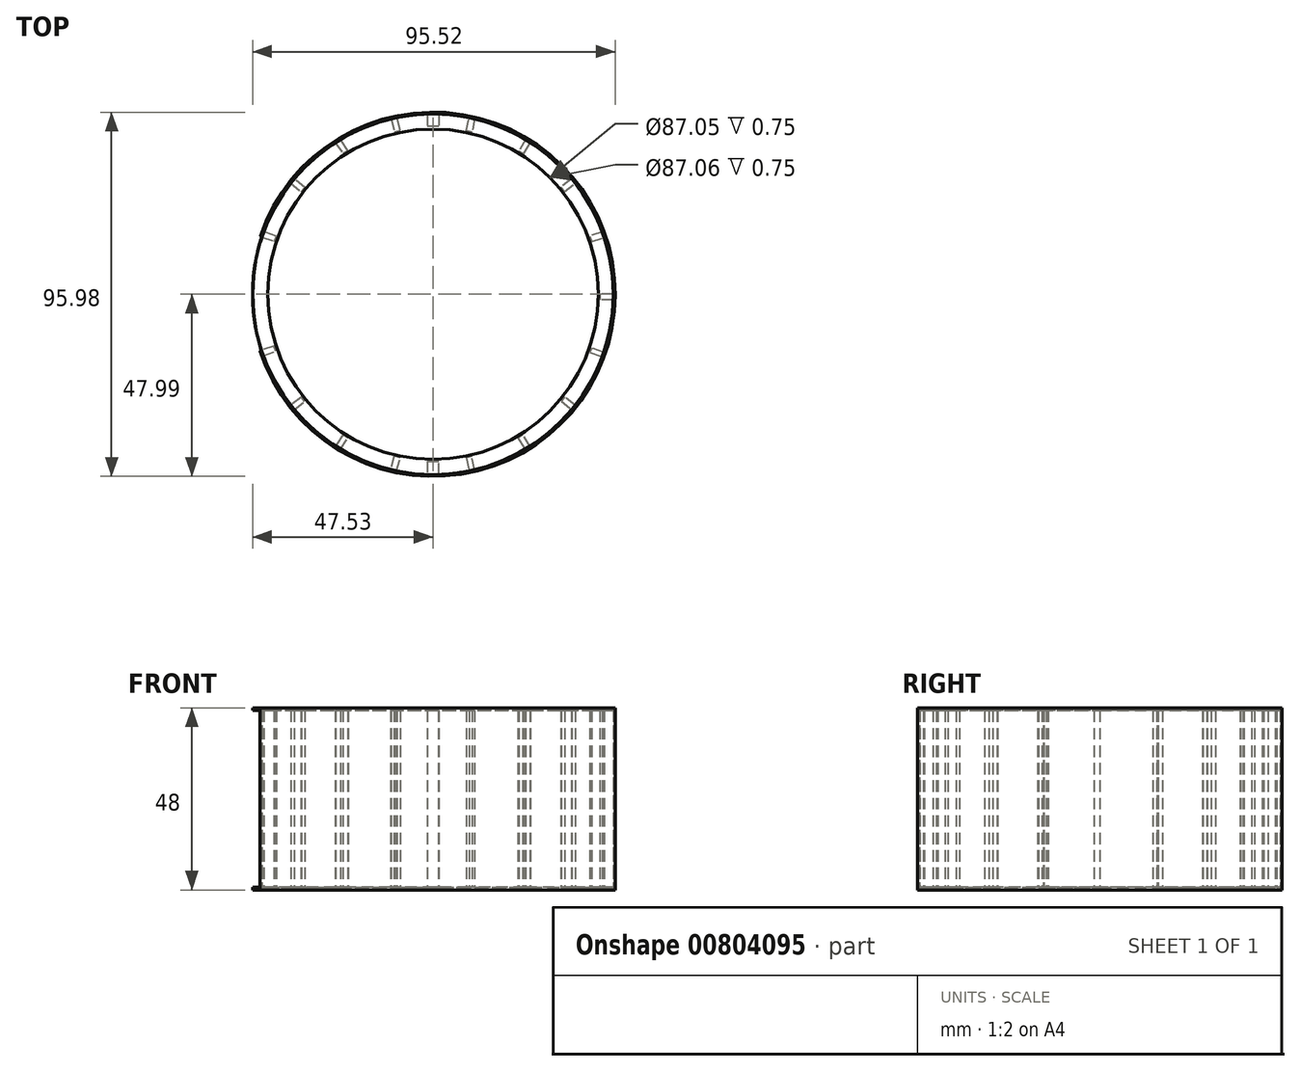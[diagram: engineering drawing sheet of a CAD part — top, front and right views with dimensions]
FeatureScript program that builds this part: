
annotation { "Feature Type Name" : "Feature", "Feature Type Description" : "" }
export const myFeature = defineFeature(function(context is Context, id is Id, definition is map)
    precondition{}
    {
        {
            var Q0;
            Q0=qCreatedBy(makeId("Front.planeOp"),FACE);
            var sketch = newSketch(context, id + "F0", { "sketchPlane" : qUnion([Q0])});
            skLineSegment(sketch, "E0", {"start": v(0, -11.28) * mm, "end": v(0, 12.82) * mm, "construction": true});
            skLineSegment(sketch, "E1", {"start": v(0, 0) * mm, "end": v(47.53, 0) * mm, "construction": true});
            skLineSegment(sketch, "E2.bottom", {"start": v(47.53, 0) * mm, "end": v(43.53, 0) * mm});
            skLineSegment(sketch, "E2.top", {"start": v(47.53, 0.75) * mm, "end": v(43.53, 0.75) * mm});
            skLineSegment(sketch, "E2.left", {"start": v(47.53, 0) * mm, "end": v(47.53, 0.75) * mm});
            skLineSegment(sketch, "E2.right", {"start": v(43.53, 0) * mm, "end": v(43.53, 0.75) * mm});
            skSolve(sketch);
        }
        {
            var Q0;
            Q0 = qSketchRegion(id + "F0", true);
            var Q1;
            Q1=sQuery(id+"F0.wireOp",EDGE,"E0");
            revolve(context, id + "F1", {"surfaceOperationType" : NewSurfaceOperationType.NEW, "entities" : qUnion([Q0]), "axis" : qUnion([Q1]), "revolveType" : RevolveType.FULL});
        }
        {
            var Q0;
            Q0=makeQuery(id+"F1.opRevolve","SWEPT_FACE",FACE,{"disambiguationData":[OSD([sQuery(id+"F0.wireOp",EDGE,"E2.top")])]});
            var sketch = newSketch(context, id + "F2", { "sketchPlane" : qUnion([Q0])});
            skLineSegment(sketch, "E3.bottom", {"start": v(0, 47.5) * mm, "end": v(1.54, 47.5) * mm});
            skLineSegment(sketch, "E3.top", {"start": v(0, 44.24) * mm, "end": v(1.54, 44.24) * mm});
            skLineSegment(sketch, "E3.left", {"start": v(0, 47.5) * mm, "end": v(0, 44.24) * mm});
            skLineSegment(sketch, "E3.right", {"start": v(1.54, 47.5) * mm, "end": v(1.54, 44.24) * mm});
            skLineSegment(sketch, "E4.bottom", {"start": v(0, 47.5) * mm, "end": v(-1.44, 47.5) * mm});
            skLineSegment(sketch, "E4.top", {"start": v(0, 44.24) * mm, "end": v(-1.44, 44.24) * mm});
            skLineSegment(sketch, "E4.right", {"start": v(-1.44, 47.5) * mm, "end": v(-1.44, 44.24) * mm});
            skLineSegment(sketch, "E5.bottom", {"start": v(0, -47.46) * mm, "end": v(1.55, -47.46) * mm});
            skLineSegment(sketch, "E5.top", {"start": v(0, -43.96) * mm, "end": v(1.55, -43.96) * mm});
            skLineSegment(sketch, "E5.left", {"start": v(0, -47.46) * mm, "end": v(0, -43.96) * mm});
            skLineSegment(sketch, "E5.right", {"start": v(1.55, -47.46) * mm, "end": v(1.55, -43.96) * mm});
            skLineSegment(sketch, "E6.bottom", {"start": v(0, -43.96) * mm, "end": v(-1.5, -43.96) * mm});
            skLineSegment(sketch, "E6.top", {"start": v(0, -47.46) * mm, "end": v(-1.5, -47.46) * mm});
            skLineSegment(sketch, "E6.left", {"start": v(0, -43.96) * mm, "end": v(0, -47.46) * mm});
            skLineSegment(sketch, "E6.right", {"start": v(-1.5, -43.96) * mm, "end": v(-1.5, -47.46) * mm});
            skLineSegment(sketch, "E7.bottom", {"start": v(47.53, 0) * mm, "end": v(44.03, 0) * mm});
            skLineSegment(sketch, "E7.top", {"start": v(47.53, -1.5) * mm, "end": v(44.03, -1.5) * mm});
            skLineSegment(sketch, "E7.left", {"start": v(47.53, 0) * mm, "end": v(47.53, -1.5) * mm});
            skLineSegment(sketch, "E7.right", {"start": v(44.03, 0) * mm, "end": v(44.03, -1.5) * mm});
            skLineSegment(sketch, "E8", {"start": v(45.02, -15.26) * mm, "end": v(41.77, -14.12) * mm});
            skLineSegment(sketch, "E9", {"start": v(41.77, -14.12) * mm, "end": v(41.35, -15.32) * mm});
            skLineSegment(sketch, "E10", {"start": v(41.35, -15.32) * mm, "end": v(44.6, -16.45) * mm});
            skLineSegment(sketch, "E11", {"start": v(44.6, -16.45) * mm, "end": v(45.02, -15.26) * mm});
            skLineSegment(sketch, "E12", {"start": v(36.53, -30.4) * mm, "end": v(37.48, -29.23) * mm});
            skLineSegment(sketch, "E13", {"start": v(37.48, -29.23) * mm, "end": v(34.7, -27.03) * mm});
            skLineSegment(sketch, "E14", {"start": v(34.7, -27.03) * mm, "end": v(33.78, -28.2) * mm});
            skLineSegment(sketch, "E15", {"start": v(33.78, -28.2) * mm, "end": v(36.53, -30.4) * mm});
            skLineSegment(sketch, "E16", {"start": v(24.28, -40.86) * mm, "end": v(25.6, -40.05) * mm});
            skLineSegment(sketch, "E17", {"start": v(25.6, -40.05) * mm, "end": v(23.7, -37.06) * mm});
            skLineSegment(sketch, "E18", {"start": v(23.7, -37.06) * mm, "end": v(22.41, -37.87) * mm});
            skLineSegment(sketch, "E19", {"start": v(22.41, -37.87) * mm, "end": v(24.28, -40.86) * mm});
            skLineSegment(sketch, "E20", {"start": v(9.5, -46.57) * mm, "end": v(11, -46.24) * mm});
            skLineSegment(sketch, "E21", {"start": v(11, -46.24) * mm, "end": v(10.25, -42.76) * mm});
            skLineSegment(sketch, "E22", {"start": v(10.25, -42.76) * mm, "end": v(8.77, -43.08) * mm});
            skLineSegment(sketch, "E23", {"start": v(8.77, -43.08) * mm, "end": v(9.5, -46.57) * mm});
            skLineSegment(sketch, "E24", {"start": v(-11.14, -46.2) * mm, "end": v(-9.6, -46.55) * mm});
            skLineSegment(sketch, "E25", {"start": v(-9.6, -46.55) * mm, "end": v(-8.65, -43.13) * mm});
            skLineSegment(sketch, "E26", {"start": v(-8.65, -43.13) * mm, "end": v(-10.27, -42.68) * mm});
            skLineSegment(sketch, "E27", {"start": v(-10.27, -42.68) * mm, "end": v(-11.14, -46.2) * mm});
            skLineSegment(sketch, "E28", {"start": v(-25.65, -40.01) * mm, "end": v(-24.35, -40.82) * mm});
            skLineSegment(sketch, "E29", {"start": v(-24.35, -40.82) * mm, "end": v(-22.39, -37.89) * mm});
            skLineSegment(sketch, "E30", {"start": v(-22.39, -37.89) * mm, "end": v(-23.67, -37.03) * mm});
            skLineSegment(sketch, "E31", {"start": v(-23.67, -37.03) * mm, "end": v(-25.65, -40.01) * mm});
            skLineSegment(sketch, "E32", {"start": v(-37.5, -29.2) * mm, "end": v(-36.51, -30.43) * mm});
            skLineSegment(sketch, "E33", {"start": v(-36.51, -30.43) * mm, "end": v(-33.74, -28.26) * mm});
            skLineSegment(sketch, "E34", {"start": v(-33.74, -28.26) * mm, "end": v(-34.65, -27.08) * mm});
            skLineSegment(sketch, "E35", {"start": v(-34.65, -27.08) * mm, "end": v(-37.5, -29.2) * mm});
            skLineSegment(sketch, "E36", {"start": v(-45.18, -14.77) * mm, "end": v(-44.68, -16.22) * mm});
            skLineSegment(sketch, "E37", {"start": v(-44.68, -16.22) * mm, "end": v(-41.35, -15.08) * mm});
            skLineSegment(sketch, "E38", {"start": v(-41.35, -15.08) * mm, "end": v(-41.84, -13.63) * mm});
            skLineSegment(sketch, "E39", {"start": v(-41.84, -13.63) * mm, "end": v(-45.18, -14.77) * mm});
            skLineSegment(sketch, "E40", {"start": v(-44.58, 16.49) * mm, "end": v(-45.08, 15.07) * mm});
            skLineSegment(sketch, "E41", {"start": v(-45.08, 15.07) * mm, "end": v(-41.75, 13.94) * mm});
            skLineSegment(sketch, "E42", {"start": v(-41.75, 13.94) * mm, "end": v(-41.27, 15.34) * mm});
            skLineSegment(sketch, "E43", {"start": v(-41.27, 15.34) * mm, "end": v(-44.58, 16.49) * mm});
            skLineSegment(sketch, "E44", {"start": v(-36.52, 30.42) * mm, "end": v(-37.46, 29.25) * mm});
            skLineSegment(sketch, "E45", {"start": v(-37.46, 29.25) * mm, "end": v(-34.74, 27) * mm});
            skLineSegment(sketch, "E46", {"start": v(-34.74, 27) * mm, "end": v(-33.78, 28.14) * mm});
            skLineSegment(sketch, "E47", {"start": v(-33.78, 28.14) * mm, "end": v(-36.52, 30.42) * mm});
            skLineSegment(sketch, "E48", {"start": v(-24.42, 40.78) * mm, "end": v(-25.7, 39.98) * mm});
            skLineSegment(sketch, "E49", {"start": v(-25.7, 39.98) * mm, "end": v(-23.7, 37.07) * mm});
            skLineSegment(sketch, "E50", {"start": v(-23.7, 37.07) * mm, "end": v(-22.45, 37.93) * mm});
            skLineSegment(sketch, "E51", {"start": v(-22.45, 37.93) * mm, "end": v(-24.42, 40.78) * mm});
            skLineSegment(sketch, "E52", {"start": v(-9.5, 46.57) * mm, "end": v(-11, 46.24) * mm});
            skLineSegment(sketch, "E53", {"start": v(-11, 46.24) * mm, "end": v(-10.12, 42.8) * mm});
            skLineSegment(sketch, "E54", {"start": v(-10.12, 42.8) * mm, "end": v(-8.66, 43.18) * mm});
            skLineSegment(sketch, "E55", {"start": v(-8.66, 43.18) * mm, "end": v(-9.5, 46.57) * mm});
            skLineSegment(sketch, "E56", {"start": v(9.5, 46.57) * mm, "end": v(10.94, 46.25) * mm});
            skLineSegment(sketch, "E57", {"start": v(10.94, 46.25) * mm, "end": v(10.27, 42.78) * mm});
            skLineSegment(sketch, "E58", {"start": v(10.27, 42.78) * mm, "end": v(8.8, 43.06) * mm});
            skLineSegment(sketch, "E59", {"start": v(8.8, 43.06) * mm, "end": v(9.5, 46.57) * mm});
            skLineSegment(sketch, "E60", {"start": v(25.7, 39.99) * mm, "end": v(24.44, 40.77) * mm});
            skLineSegment(sketch, "E61", {"start": v(24.44, 40.77) * mm, "end": v(22.63, 37.73) * mm});
            skLineSegment(sketch, "E62", {"start": v(22.63, 37.73) * mm, "end": v(23.93, 36.95) * mm});
            skLineSegment(sketch, "E63", {"start": v(23.93, 36.95) * mm, "end": v(25.7, 39.99) * mm});
            skLineSegment(sketch, "E64", {"start": v(37.45, 29.26) * mm, "end": v(36.5, 30.43) * mm});
            skLineSegment(sketch, "E65", {"start": v(36.5, 30.43) * mm, "end": v(33.72, 28.29) * mm});
            skLineSegment(sketch, "E66", {"start": v(33.72, 28.29) * mm, "end": v(34.64, 27.09) * mm});
            skLineSegment(sketch, "E67", {"start": v(34.64, 27.09) * mm, "end": v(37.45, 29.26) * mm});
            skLineSegment(sketch, "E68", {"start": v(45.11, 14.97) * mm, "end": v(44.6, 16.45) * mm});
            skLineSegment(sketch, "E69", {"start": v(44.6, 16.45) * mm, "end": v(41.26, 15.32) * mm});
            skLineSegment(sketch, "E70", {"start": v(41.26, 15.32) * mm, "end": v(41.74, 13.9) * mm});
            skLineSegment(sketch, "E71", {"start": v(41.74, 13.9) * mm, "end": v(45.11, 14.97) * mm});
            skLineSegment(sketch, "E72.bottom", {"start": v(44.03, 0) * mm, "end": v(47.5, 0) * mm});
            skLineSegment(sketch, "E72.top", {"start": v(44.03, 1.5) * mm, "end": v(47.5, 1.5) * mm});
            skLineSegment(sketch, "E72.left", {"start": v(44.03, 0) * mm, "end": v(44.03, 1.5) * mm});
            skLineSegment(sketch, "E72.right", {"start": v(47.5, 0) * mm, "end": v(47.5, 1.5) * mm});
            skSolve(sketch);
        }
        {
            var Q0;
            Q0=makeQuery(id+"F2.imprint","IMPRINT",FACE,{"disambiguationData":[TD([[makeQuery(id+"F2.imprint","IMPRINT",EDGE,{"derivedFrom":sQuery(id+"F2.wireOp",EDGE,"E40")}),1.0]])]});
            var Q1;
            Q1=makeQuery(id+"F2.imprint","IMPRINT",FACE,{"disambiguationData":[TD([[makeQuery(id+"F2.imprint","IMPRINT",EDGE,{"derivedFrom":sQuery(id+"F2.wireOp",EDGE,"E44")}),1.0]])]});
            var Q2;
            Q2=makeQuery(id+"F2.imprint","IMPRINT",FACE,{"disambiguationData":[TD([[makeQuery(id+"F2.imprint","IMPRINT",EDGE,{"derivedFrom":sQuery(id+"F2.wireOp",EDGE,"E48")}),1.0]])]});
            var Q3;
            Q3=makeQuery(id+"F2.imprint","IMPRINT",FACE,{"disambiguationData":[TD([[makeQuery(id+"F2.imprint","IMPRINT",EDGE,{"derivedFrom":sQuery(id+"F2.wireOp",EDGE,"E52")}),1.0]])]});
            var Q4;
            Q4=makeQuery(id+"F2.imprint","IMPRINT",FACE,{"disambiguationData":[TD([[makeQuery(id+"F2.imprint","IMPRINT",EDGE,{"derivedFrom":sQuery(id+"F2.wireOp",EDGE,"E4.bottom")}),1.0]])]});
            var Q5;
            {var subQ1=sQuery(id+"F2.wireOp",EDGE,"E3.top");Q5=makeQuery(id+"F2.imprint","IMPRINT",FACE,{"disambiguationData":[TD([[makeQuery(id+"F2.imprint","IMPRINT",EDGE,{"derivedFrom":subQ1}),1.0]])]});}
            var Q6;
            Q6=makeQuery(id+"F2.imprint","IMPRINT",FACE,{"disambiguationData":[TD([[makeQuery(id+"F2.imprint","IMPRINT",EDGE,{"derivedFrom":sQuery(id+"F2.wireOp",EDGE,"E56")}),-1.0]])]});
            var Q7;
            Q7=makeQuery(id+"F2.imprint","IMPRINT",FACE,{"disambiguationData":[TD([[makeQuery(id+"F2.imprint","IMPRINT",EDGE,{"derivedFrom":sQuery(id+"F2.wireOp",EDGE,"E60")}),1.0]])]});
            var Q8;
            Q8=makeQuery(id+"F2.imprint","IMPRINT",FACE,{"disambiguationData":[TD([[makeQuery(id+"F2.imprint","IMPRINT",EDGE,{"derivedFrom":sQuery(id+"F2.wireOp",EDGE,"E64")}),1.0]])]});
            var Q9;
            Q9=makeQuery(id+"F2.imprint","IMPRINT",FACE,{"disambiguationData":[TD([[makeQuery(id+"F2.imprint","IMPRINT",EDGE,{"derivedFrom":sQuery(id+"F2.wireOp",EDGE,"E68")}),1.0]])]});
            var Q10;
            Q10=makeQuery(id+"F2.imprint","IMPRINT",FACE,{"disambiguationData":[TD([[makeQuery(id+"F2.imprint","IMPRINT",EDGE,{"derivedFrom":sQuery(id+"F2.wireOp",EDGE,"E72.bottom")}),1.0]])]});
            var Q11;
            {var subQ4=sQuery(id+"F2.wireOp",EDGE,"E7.bottom");Q11=makeQuery(id+"F2.imprint","IMPRINT",FACE,{"disambiguationData":[TD([[makeQuery(id+"F2.imprint","IMPRINT",EDGE,{"derivedFrom":subQ4}),1.0]])]});}
            var Q12;
            Q12=makeQuery(id+"F2.imprint","IMPRINT",FACE,{"disambiguationData":[TD([[makeQuery(id+"F2.imprint","IMPRINT",EDGE,{"derivedFrom":sQuery(id+"F2.wireOp",EDGE,"E8")}),1.0]])]});
            var Q13;
            Q13=makeQuery(id+"F2.imprint","IMPRINT",FACE,{"disambiguationData":[TD([[makeQuery(id+"F2.imprint","IMPRINT",EDGE,{"derivedFrom":sQuery(id+"F2.wireOp",EDGE,"E12")}),1.0]])]});
            var Q14;
            Q14=makeQuery(id+"F2.imprint","IMPRINT",FACE,{"disambiguationData":[TD([[makeQuery(id+"F2.imprint","IMPRINT",EDGE,{"derivedFrom":sQuery(id+"F2.wireOp",EDGE,"E16")}),1.0]])]});
            var Q15;
            Q15=makeQuery(id+"F2.imprint","IMPRINT",FACE,{"disambiguationData":[TD([[makeQuery(id+"F2.imprint","IMPRINT",EDGE,{"derivedFrom":sQuery(id+"F2.wireOp",EDGE,"E20")}),1.0]])]});
            var Q16;
            Q16=makeQuery(id+"F2.imprint","IMPRINT",FACE,{"disambiguationData":[TD([[makeQuery(id+"F2.imprint","IMPRINT",EDGE,{"derivedFrom":sQuery(id+"F2.wireOp",EDGE,"E5.bottom")}),1.0]])]});
            var Q17;
            Q17=makeQuery(id+"F2.imprint","IMPRINT",FACE,{"disambiguationData":[TD([[makeQuery(id+"F2.imprint","IMPRINT",EDGE,{"derivedFrom":sQuery(id+"F2.wireOp",EDGE,"E6.bottom")}),1.0]])]});
            var Q18;
            Q18=makeQuery(id+"F2.imprint","IMPRINT",FACE,{"disambiguationData":[TD([[makeQuery(id+"F2.imprint","IMPRINT",EDGE,{"derivedFrom":sQuery(id+"F2.wireOp",EDGE,"E24")}),1.0]])]});
            var Q19;
            Q19=makeQuery(id+"F2.imprint","IMPRINT",FACE,{"disambiguationData":[TD([[makeQuery(id+"F2.imprint","IMPRINT",EDGE,{"derivedFrom":sQuery(id+"F2.wireOp",EDGE,"E28")}),1.0]])]});
            var Q20;
            Q20=makeQuery(id+"F2.imprint","IMPRINT",FACE,{"disambiguationData":[TD([[makeQuery(id+"F2.imprint","IMPRINT",EDGE,{"derivedFrom":sQuery(id+"F2.wireOp",EDGE,"E32")}),1.0]])]});
            var Q21;
            Q21=makeQuery(id+"F2.imprint","IMPRINT",FACE,{"disambiguationData":[TD([[makeQuery(id+"F2.imprint","IMPRINT",EDGE,{"derivedFrom":sQuery(id+"F2.wireOp",EDGE,"E36")}),1.0]])]});
            extrude(context, id + "F3", {"entities" : qUnion([Q0, Q1, Q2, Q3, Q4, Q5, Q6, Q7, Q8, Q9, Q10, Q11, Q12, Q13, Q14, Q15, Q16, Q17, Q18, Q19, Q20, Q21]), "operationType" : NewBodyOperationType.ADD, "depth" : 46.5 * mm, "offsetDistance" : 25 * mm});
        }
        {
            var Q0;
            Q0=qCreatedBy(makeId("Front.planeOp"),FACE);
            var sketch = newSketch(context, id + "F4", { "sketchPlane" : qUnion([Q0])});
            skLineSegment(sketch, "E73.bottom", {"start": v(47.53, 47.25) * mm, "end": v(43.53, 47.25) * mm});
            skLineSegment(sketch, "E73.top", {"start": v(47.53, 48) * mm, "end": v(43.53, 48) * mm});
            skLineSegment(sketch, "E73.left", {"start": v(47.53, 47.25) * mm, "end": v(47.53, 48) * mm});
            skLineSegment(sketch, "E73.right", {"start": v(43.53, 47.25) * mm, "end": v(43.53, 48) * mm});
            skSolve(sketch);
        }
        {
            var Q0;
            Q0 = qSketchRegion(id + "F4", true);
            var Q1;
            Q1=sQuery(id+"F0.wireOp",EDGE,"E0");
            revolve(context, id + "F5", {"surfaceOperationType" : NewSurfaceOperationType.NEW, "entities" : qUnion([Q0]), "axis" : qUnion([Q1]), "revolveType" : RevolveType.FULL});
        }
        {
            var Q0;
            Q0=qCreatedBy(makeId("Top.planeOp"),FACE);
            var sketch = newSketch(context, id + "F6", { "sketchPlane" : qUnion([Q0])});
            skArc(sketch, "E74", {"start": v(-45.22, -14.8) * mm, "mid": v(47.57, -0.16) * mm, "end": v(-45.12, 15.1) * mm});
            skArc(sketch, "E75", {"start": v(-45.35, -14.8) * mm, "mid": v(47.7, -0.18) * mm, "end": v(-45.24, 15.14) * mm});
            skLineSegment(sketch, "E76", {"start": v(-45.24, 15.14) * mm, "end": v(-45.12, 15.1) * mm});
            skLineSegment(sketch, "E77", {"start": v(-45.35, -14.8) * mm, "end": v(-45.22, -14.8) * mm});
            skSolve(sketch);
        }
        {
            var Q0;
            Q0=makeQuery(id+"F6.imprint","IMPRINT",FACE,{"disambiguationData":[TD([[makeQuery(id+"F6.imprint","IMPRINT",EDGE,{"derivedFrom":sQuery(id+"F6.wireOp",EDGE,"E74")}),-1.0]])]});
            extrude(context, id + "F7", {"entities" : qUnion([Q0]), "depth" : 48 * mm, "offsetDistance" : 25 * mm});
        }
        {
            var Q0;
            Q0=qCreatedBy(makeId("Top.planeOp"),FACE);
            var sketch = newSketch(context, id + "F8", { "sketchPlane" : qUnion([Q0])});
            skArc(sketch, "E78", {"start": v(-45.39, -14.8) * mm, "mid": v(47.74, -0.18) * mm, "end": v(-45.27, 15.14) * mm});
            skArc(sketch, "E79", {"start": v(-45.62, -14.9) * mm, "mid": v(48, -0.2) * mm, "end": v(-45.5, 15.28) * mm});
            skLineSegment(sketch, "E80", {"start": v(-45.5, 15.28) * mm, "end": v(-45.27, 15.14) * mm});
            skLineSegment(sketch, "E81", {"start": v(-45.62, -14.9) * mm, "end": v(-45.39, -14.8) * mm});
            skSolve(sketch);
        }
        {
            var Q0;
            Q0=makeQuery(id+"F8.imprint","IMPRINT",FACE,{"disambiguationData":[TD([[makeQuery(id+"F8.imprint","IMPRINT",EDGE,{"derivedFrom":sQuery(id+"F8.wireOp",EDGE,"E78")}),-1.0]])]});
            extrude(context, id + "F9", {"entities" : qUnion([Q0]), "depth" : 48 * mm, "offsetDistance" : 25 * mm});
        }
    });
